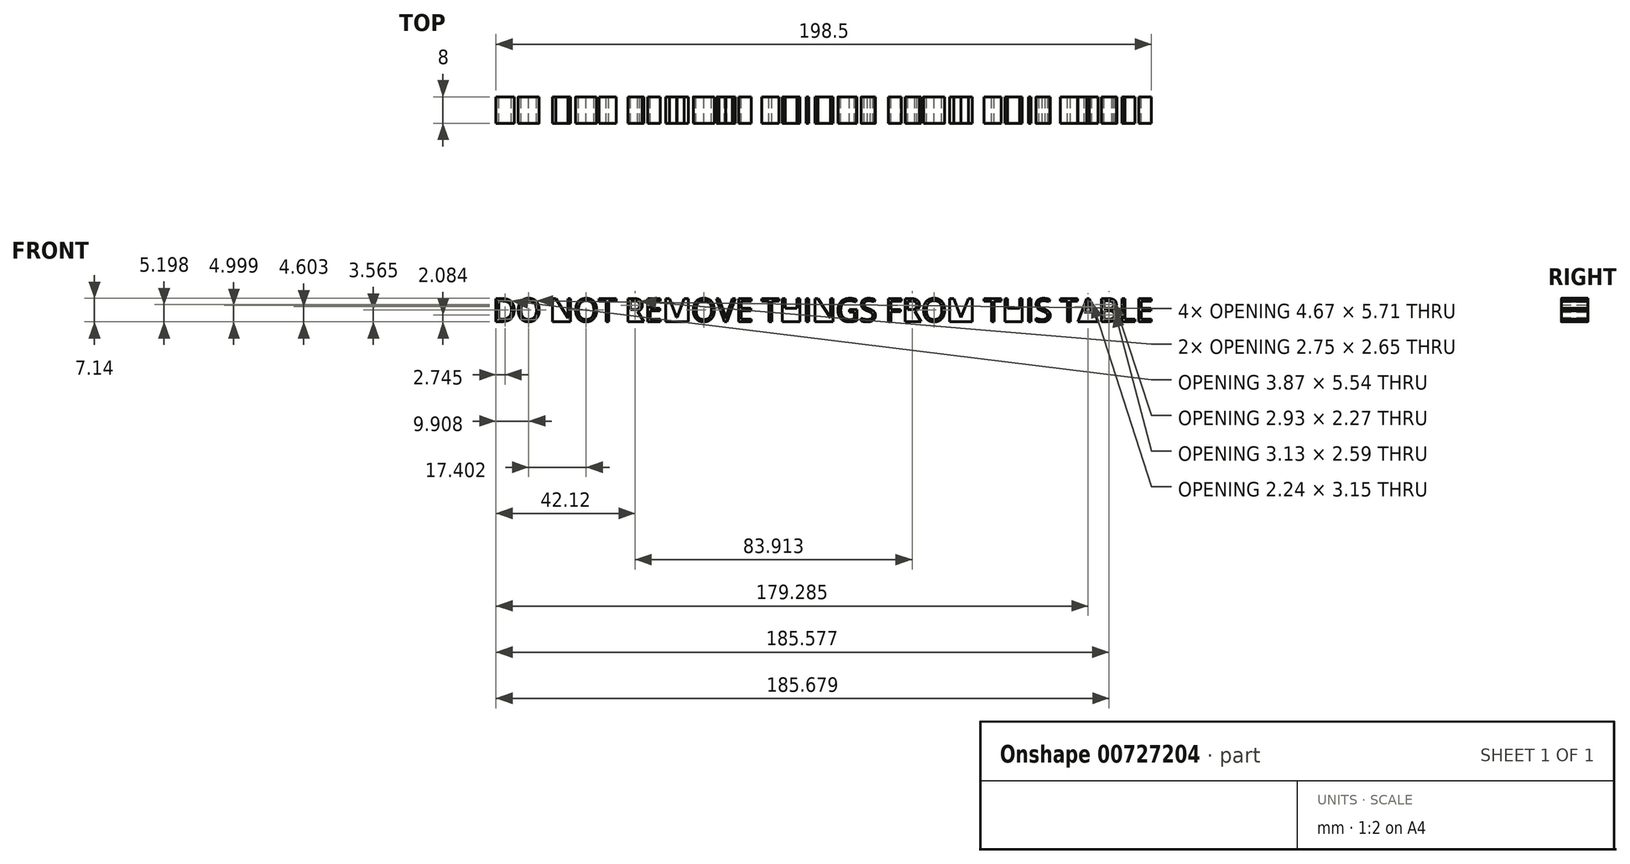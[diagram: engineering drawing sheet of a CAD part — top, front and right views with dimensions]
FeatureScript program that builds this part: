
annotation { "Feature Type Name" : "Feature", "Feature Type Description" : "" }
export const myFeature = defineFeature(function(context is Context, id is Id, definition is map)
    precondition{}
    {
        {
            var Q0;
            Q0=qCreatedBy(makeId("Front.planeOp"),FACE);
            var sketch = newSketch(context, id + "F0", { "sketchPlane" : qUnion([Q0])});
            skText(sketch, "E0", { "text": "DO NOT REMOVE THINGS FROM THIS TABLE", "fontName": "OpenSans-Regular.ttf"});
            skLineSegment(sketch, "E1.bottom", {"start": v(100, 1.5) * mm, "end": v(-100, 1.5) * mm});
            skLineSegment(sketch, "E1.left", {"start": v(100, 1.5) * mm, "end": v(100, 0) * mm});
            skLineSegment(sketch, "E1.right", {"start": v(-100, 1.5) * mm, "end": v(-100, 0) * mm});
            const initialGuessF0  = {"E0": [-0.1, 0.0015, 1, 0, 0.00699]};
            skSetInitialGuess(sketch, initialGuessF0);
            skSolve(sketch);
        }
        {
            var Q0;
            Q0 = qSketchRegion(id + "F0", true);
            extrude(context, id + "F1", {"entities" : qUnion([Q0]), "depth" : 8 * mm, "offsetDistance" : 25.4 * mm});
        }
    });
